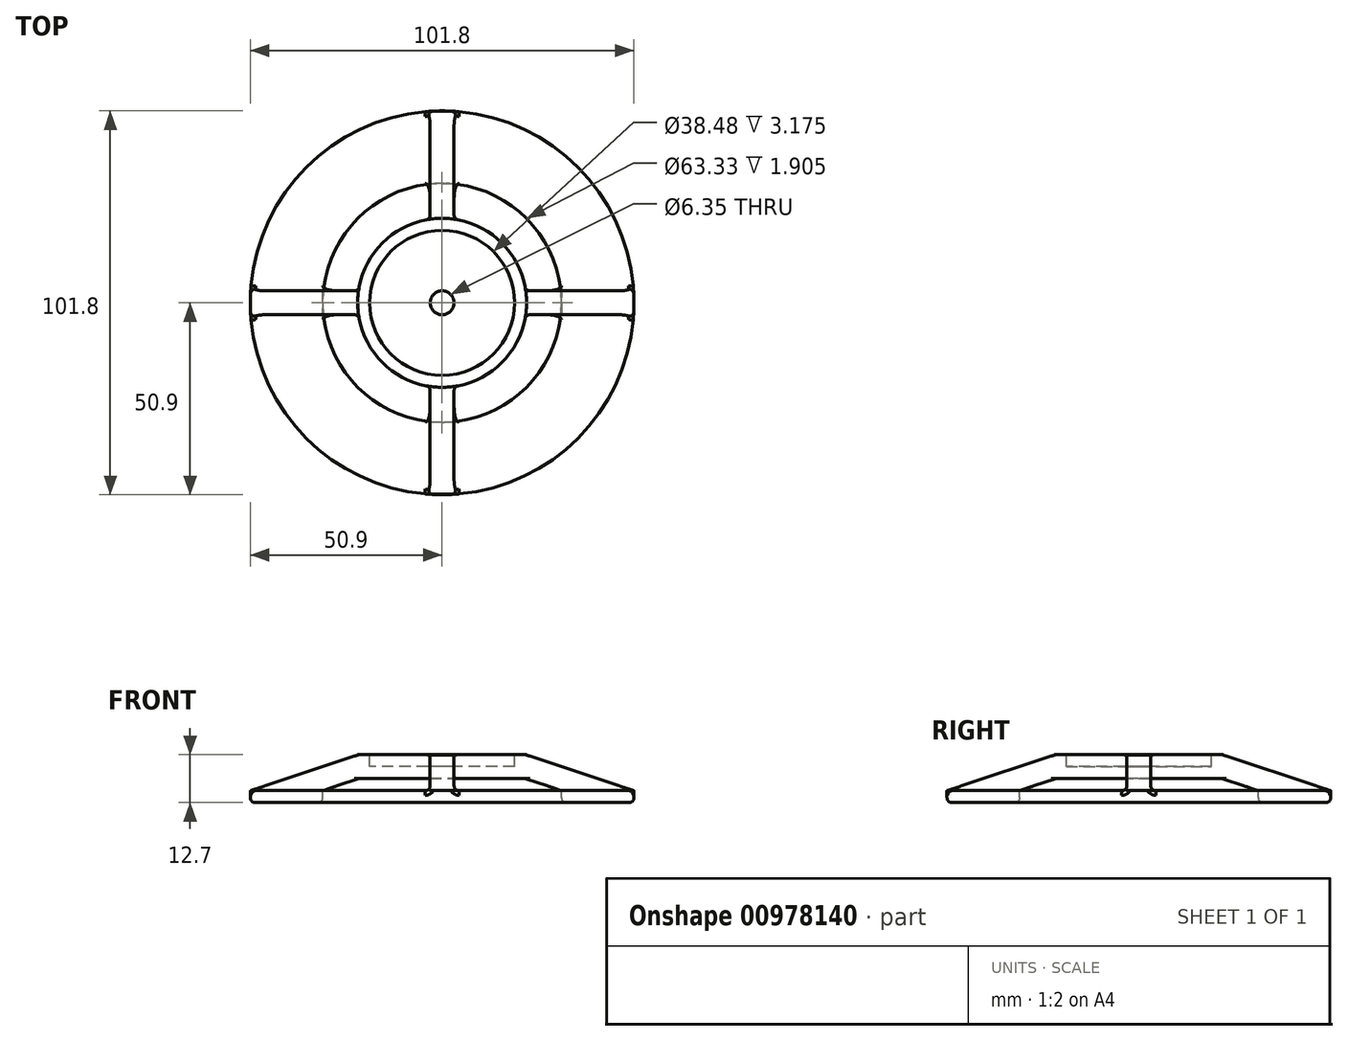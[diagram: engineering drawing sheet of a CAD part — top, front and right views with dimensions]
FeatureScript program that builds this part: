
annotation { "Feature Type Name" : "Feature", "Feature Type Description" : "" }
export const myFeature = defineFeature(function(context is Context, id is Id, definition is map)
    precondition{}
    {
        {
            var Q0;
            Q0=qCreatedBy(makeId("Top.planeOp"),FACE);
            var sketch = newSketch(context, id + "F0", { "sketchPlane" : qUnion([Q0])});
            skCircle(sketch, "E0", {"center": v(0, 0) * mm, "radius": 22.42 * mm});
            skSolve(sketch);
        }
        {
            var Q0;
            Q0 = qSketchRegion(id + "F0", true);
            extrude(context, id + "F1", {"entities" : qUnion([Q0]), "depth" : 6.35 * mm, "offsetDistance" : 25.4 * mm});
        }
        {
            var Q0;
            Q0=makeQuery(id+"F1.opExtrude","CAP_FACE",FACE,{"disambiguationData":[OSD([sQuery(id+"F0.wireOp",EDGE,"E0")])],"isStart":false});
            var sketch = newSketch(context, id + "F2", { "sketchPlane" : qUnion([Q0])});
            skCircle(sketch, "E1", {"center": v(0, 0) * mm, "radius": 19.24 * mm});
            skSolve(sketch);
        }
        {
            var Q0;
            Q0 = qSketchRegion(id + "F2", true);
            extrude(context, id + "F3", {"entities" : qUnion([Q0]), "operationType" : NewBodyOperationType.REMOVE, "oppositeDirection" : true, "depth" : 3.17 * mm, "offsetDistance" : 25.4 * mm});
        }
        {
            var Q0;
            Q0=qCreatedBy(makeId("Front.planeOp"),FACE);
            var sketch = newSketch(context, id + "F4", { "sketchPlane" : qUnion([Q0])});
            skLineSegment(sketch, "E2", {"start": v(-22.1, 6.35) * mm, "end": v(-50.8, -3.18) * mm});
            skLineSegment(sketch, "E3", {"start": v(-50.8, -3.18) * mm, "end": v(-31.67, -3.18) * mm});
            skLineSegment(sketch, "E4", {"start": v(-31.67, -3.18) * mm, "end": v(-22.1, 0) * mm});
            skLineSegment(sketch, "E5", {"start": v(-22.1, 0) * mm, "end": v(-22.1, 6.35) * mm});
            skSolve(sketch);
        }
        {
            var Q0;
            Q0 = qSketchRegion(id + "F4", true);
            extrude(context, id + "F5", {"entities" : qUnion([Q0]), "operationType" : NewBodyOperationType.ADD, "endBound" : BoundingType.SYMMETRIC, "depth" : 6.35 * mm, "offsetDistance" : 25.4 * mm});
        }
        {
            var Q0;
            Q0=qCreatedBy(makeId("Front.planeOp"),FACE);
            var sketch = newSketch(context, id + "F6", { "sketchPlane" : qUnion([Q0])});
            skLineSegment(sketch, "E6", {"start": v(0, 0) * mm, "end": v(0, 12.7) * mm, "construction": true});
            skSolve(sketch);
        }
        {
            var Q0;
            Q0=makeQuery(id+"F1.opExtrude","SWEPT_BODY",BODY,{"disambiguationData":[OSD([sQuery(id+"F0.wireOp",EDGE,"E0")])]});
            var Q1;
            Q1=sQuery(id+"F6.wireOp",EDGE,"E6");
            circularPattern(context, id + "F7", {"entities" : qUnion([Q0]), "axis" : qUnion([Q1]), "angle" : 360 * degree, "instanceCount" : 4, "equalSpace" : true});
        }
        {
            var Q0;
            Q0=makeQuery(id+"F5.opExtrude","SWEPT_FACE",FACE,{"disambiguationData":[OSD([sQuery(id+"F4.wireOp",EDGE,"E3")])]});
            var sketch = newSketch(context, id + "F8", { "sketchPlane" : qUnion([Q0])});
            skCircle(sketch, "E7", {"center": v(0, 0) * mm, "radius": 50.9 * mm});
            skCircle(sketch, "E8", {"center": v(0, 0) * mm, "radius": 31.67 * mm});
            skSolve(sketch);
        }
        {
            var Q0;
            Q0 = qSketchRegion(id + "F8", true);
            extrude(context, id + "F9", {"entities" : qUnion([Q0]), "operationType" : NewBodyOperationType.ADD, "depth" : 3.17 * mm, "offsetDistance" : 25.4 * mm});
        }
        {
            var Q0;
            Q0=makeQuery(id+"F3.boolean.opBoolean","COPY",FACE,{"derivedFrom":makeQuery(id+"F3.opExtrude","CAP_FACE",FACE,{"disambiguationData":[OSD([sQuery(id+"F2.wireOp",EDGE,"E1")])],"isStart":false})});
            var sketch = newSketch(context, id + "F10", { "sketchPlane" : qUnion([Q0])});
            skCircle(sketch, "E9", {"center": v(0, 0) * mm, "radius": 3.18 * mm});
            skSolve(sketch);
        }
        {
            var Q0;
            Q0 = qSketchRegion(id + "F10", true);
            extrude(context, id + "F11", {"entities" : qUnion([Q0]), "operationType" : NewBodyOperationType.REMOVE, "endBound" : BoundingType.THROUGH_ALL, "oppositeDirection" : true, "depth" : 25.4 * mm, "offsetDistance" : 25.4 * mm});
        }
        {
            var Q0;
            Q0=makeQuery(id+"F3.boolean.opBoolean","COPY",EDGE,{"derivedFrom":makeQuery(id+"F3.opExtrude","CAP_EDGE",EDGE,{"disambiguationData":[OSD([sQuery(id+"F2.wireOp",EDGE,"E1")])],"isStart":true})});
            var Q1;
            Q1=makeQuery(id+"F5.opExtrude","CAP_EDGE",EDGE,{"disambiguationData":[OSD([sQuery(id+"F4.wireOp",EDGE,"E3")])],"isStart":false});
            var Q2;
            Q2=makeQuery(id+"F7.opPattern","COPY",EDGE,{"derivedFrom":makeQuery(id+"F5.opExtrude","CAP_EDGE",EDGE,{"disambiguationData":[OSD([sQuery(id+"F4.wireOp",EDGE,"E3")])],"isStart":true}),"instanceName":"1"});
            var Q3;
            Q3=makeQuery(id+"F7.opPattern","COPY",EDGE,{"derivedFrom":makeQuery(id+"F5.opExtrude","CAP_EDGE",EDGE,{"disambiguationData":[OSD([sQuery(id+"F4.wireOp",EDGE,"E3")])],"isStart":false}),"instanceName":"1"});
            var Q4;
            Q4=makeQuery(id+"F7.opPattern","COPY",EDGE,{"derivedFrom":makeQuery(id+"F5.opExtrude","CAP_EDGE",EDGE,{"disambiguationData":[OSD([sQuery(id+"F4.wireOp",EDGE,"E3")])],"isStart":true}),"instanceName":"2"});
            var Q5;
            {var subQ0=makeQuery(id+"F1.opExtrude","SWEPT_FACE",FACE,{"disambiguationData":[OSD([sQuery(id+"F0.wireOp",EDGE,"E0")])]});var subQ1=subQ0;Q5=makeQuery(id+"F9.boolean.opBoolean","INTERSECT",EDGE,{"disambiguationData":[topologyDisambiguationEdgeConnected([makeQuery(id+"F7.opPattern","COPY",FACE,{"derivedFrom":makeQuery(id+"F5.opExtrude","CAP_FACE",FACE,{"disambiguationData":[OSD([sQuery(id+"F4.wireOp",EDGE,"E2"),sQuery(id+"F4.wireOp",EDGE,"E3"),sQuery(id+"F4.wireOp",EDGE,"E4"),sQuery(id+"F4.wireOp",EDGE,"E5")])],"isStart":true}),"instanceName":"2"})])],"derivedFrom":[subQ1,makeQuery(id+"F7.opPattern","COPY",FACE,{"derivedFrom":subQ1,"instanceName":"1"}),makeQuery(id+"F7.opPattern","COPY",FACE,{"derivedFrom":subQ1,"instanceName":"3"})]});}
            var Q6;
            {var subQ0=makeQuery(id+"F1.opExtrude","SWEPT_FACE",FACE,{"disambiguationData":[OSD([sQuery(id+"F0.wireOp",EDGE,"E0")])]});var subQ1=subQ0;Q6=makeQuery(id+"F9.boolean.opBoolean","INTERSECT",EDGE,{"disambiguationData":[topologyDisambiguationEdgeConnected([makeQuery(id+"F7.opPattern","COPY",FACE,{"derivedFrom":makeQuery(id+"F5.opExtrude","CAP_FACE",FACE,{"disambiguationData":[OSD([sQuery(id+"F4.wireOp",EDGE,"E2"),sQuery(id+"F4.wireOp",EDGE,"E3"),sQuery(id+"F4.wireOp",EDGE,"E4"),sQuery(id+"F4.wireOp",EDGE,"E5")])],"isStart":false}),"instanceName":"1"})])],"derivedFrom":[subQ1,makeQuery(id+"F7.opPattern","COPY",FACE,{"derivedFrom":subQ1,"instanceName":"2"})]});}
            var Q7;
            Q7=makeQuery(id+"F5.boolean.opBoolean","INTERSECT",EDGE,{"derivedFrom":[makeQuery(id+"F1.opExtrude","SWEPT_FACE",FACE,{"disambiguationData":[OSD([sQuery(id+"F0.wireOp",EDGE,"E0")])]}),makeQuery(id+"F5.opExtrude","CAP_FACE",FACE,{"disambiguationData":[OSD([sQuery(id+"F4.wireOp",EDGE,"E2"),sQuery(id+"F4.wireOp",EDGE,"E3"),sQuery(id+"F4.wireOp",EDGE,"E4"),sQuery(id+"F4.wireOp",EDGE,"E5")])],"isStart":false})]});
            var Q8;
            {var subQ0=makeQuery(id+"F1.opExtrude","SWEPT_FACE",FACE,{"disambiguationData":[OSD([sQuery(id+"F0.wireOp",EDGE,"E0")])]});var subQ1=subQ0;Q8=makeQuery(id+"F9.boolean.opBoolean","INTERSECT",EDGE,{"disambiguationData":[topologyDisambiguationEdgeConnected([makeQuery(id+"F7.opPattern","COPY",FACE,{"derivedFrom":makeQuery(id+"F5.opExtrude","CAP_FACE",FACE,{"disambiguationData":[OSD([sQuery(id+"F4.wireOp",EDGE,"E2"),sQuery(id+"F4.wireOp",EDGE,"E3"),sQuery(id+"F4.wireOp",EDGE,"E4"),sQuery(id+"F4.wireOp",EDGE,"E5")])],"isStart":true}),"instanceName":"1"})])],"derivedFrom":[subQ1,makeQuery(id+"F7.opPattern","COPY",FACE,{"derivedFrom":subQ1,"instanceName":"2"})]});}
            var Q9;
            Q9=makeQuery(id+"F5.boolean.opBoolean","INTERSECT",EDGE,{"derivedFrom":[makeQuery(id+"F1.opExtrude","SWEPT_FACE",FACE,{"disambiguationData":[OSD([sQuery(id+"F0.wireOp",EDGE,"E0")])]}),makeQuery(id+"F5.opExtrude","CAP_FACE",FACE,{"disambiguationData":[OSD([sQuery(id+"F4.wireOp",EDGE,"E2"),sQuery(id+"F4.wireOp",EDGE,"E3"),sQuery(id+"F4.wireOp",EDGE,"E4"),sQuery(id+"F4.wireOp",EDGE,"E5")])],"isStart":true})]});
            var Q10;
            Q10=makeQuery(id+"F5.opExtrude","CAP_EDGE",EDGE,{"disambiguationData":[OSD([sQuery(id+"F4.wireOp",EDGE,"E3")])],"isStart":true});
            var Q11;
            {var subQ0=makeQuery(id+"F1.opExtrude","SWEPT_FACE",FACE,{"disambiguationData":[OSD([sQuery(id+"F0.wireOp",EDGE,"E0")])]});var subQ1=subQ0;Q11=makeQuery(id+"F9.boolean.opBoolean","INTERSECT",EDGE,{"disambiguationData":[topologyDisambiguationEdgeConnected([makeQuery(id+"F7.opPattern","COPY",FACE,{"derivedFrom":makeQuery(id+"F5.opExtrude","CAP_FACE",FACE,{"disambiguationData":[OSD([sQuery(id+"F4.wireOp",EDGE,"E2"),sQuery(id+"F4.wireOp",EDGE,"E3"),sQuery(id+"F4.wireOp",EDGE,"E4"),sQuery(id+"F4.wireOp",EDGE,"E5")])],"isStart":false}),"instanceName":"3"})])],"derivedFrom":[subQ1,makeQuery(id+"F7.opPattern","COPY",FACE,{"derivedFrom":subQ1,"instanceName":"1"}),makeQuery(id+"F7.opPattern","COPY",FACE,{"derivedFrom":subQ1,"instanceName":"2"})]});}
            var Q12;
            Q12=makeQuery(id+"F7.opPattern","COPY",EDGE,{"derivedFrom":makeQuery(id+"F5.opExtrude","CAP_EDGE",EDGE,{"disambiguationData":[OSD([sQuery(id+"F4.wireOp",EDGE,"E3")])],"isStart":false}),"instanceName":"3"});
            var Q13;
            {var subQ0=makeQuery(id+"F1.opExtrude","SWEPT_FACE",FACE,{"disambiguationData":[OSD([sQuery(id+"F0.wireOp",EDGE,"E0")])]});var subQ1=subQ0;Q13=makeQuery(id+"F9.boolean.opBoolean","INTERSECT",EDGE,{"disambiguationData":[topologyDisambiguationEdgeConnected([makeQuery(id+"F7.opPattern","COPY",FACE,{"derivedFrom":makeQuery(id+"F5.opExtrude","CAP_FACE",FACE,{"disambiguationData":[OSD([sQuery(id+"F4.wireOp",EDGE,"E2"),sQuery(id+"F4.wireOp",EDGE,"E3"),sQuery(id+"F4.wireOp",EDGE,"E4"),sQuery(id+"F4.wireOp",EDGE,"E5")])],"isStart":true}),"instanceName":"3"})])],"derivedFrom":[subQ1,makeQuery(id+"F7.opPattern","COPY",FACE,{"derivedFrom":subQ1,"instanceName":"1"}),makeQuery(id+"F7.opPattern","COPY",FACE,{"derivedFrom":subQ1,"instanceName":"2"})]});}
            var Q14;
            Q14=makeQuery(id+"F7.opPattern","COPY",EDGE,{"derivedFrom":makeQuery(id+"F5.opExtrude","CAP_EDGE",EDGE,{"disambiguationData":[OSD([sQuery(id+"F4.wireOp",EDGE,"E3")])],"isStart":true}),"instanceName":"3"});
            var Q15;
            {var subQ0=makeQuery(id+"F1.opExtrude","SWEPT_FACE",FACE,{"disambiguationData":[OSD([sQuery(id+"F0.wireOp",EDGE,"E0")])]});var subQ1=subQ0;Q15=makeQuery(id+"F9.boolean.opBoolean","INTERSECT",EDGE,{"disambiguationData":[topologyDisambiguationEdgeConnected([makeQuery(id+"F7.opPattern","COPY",FACE,{"derivedFrom":makeQuery(id+"F5.opExtrude","CAP_FACE",FACE,{"disambiguationData":[OSD([sQuery(id+"F4.wireOp",EDGE,"E2"),sQuery(id+"F4.wireOp",EDGE,"E3"),sQuery(id+"F4.wireOp",EDGE,"E4"),sQuery(id+"F4.wireOp",EDGE,"E5")])],"isStart":false}),"instanceName":"2"})])],"derivedFrom":[subQ1,makeQuery(id+"F7.opPattern","COPY",FACE,{"derivedFrom":subQ1,"instanceName":"1"}),makeQuery(id+"F7.opPattern","COPY",FACE,{"derivedFrom":subQ1,"instanceName":"3"})]});}
            var Q16;
            Q16=makeQuery(id+"F7.opPattern","COPY",EDGE,{"derivedFrom":makeQuery(id+"F5.opExtrude","CAP_EDGE",EDGE,{"disambiguationData":[OSD([sQuery(id+"F4.wireOp",EDGE,"E3")])],"isStart":false}),"instanceName":"2"});
            var Q17;
            Q17=makeQuery(id+"F11.boolean.opBoolean","INTERSECT",EDGE,{"derivedFrom":[makeQuery(id+"F1.opExtrude","CAP_FACE",FACE,{"disambiguationData":[OSD([sQuery(id+"F0.wireOp",EDGE,"E0")])],"isStart":true}),makeQuery(id+"F11.opExtrude","SWEPT_FACE",FACE,{"disambiguationData":[OSD([sQuery(id+"F10.wireOp",EDGE,"E9")])]})]});
            var Q18;
            {var subQ0=makeQuery(id+"F1.opExtrude","CAP_FACE",FACE,{"disambiguationData":[OSD([sQuery(id+"F0.wireOp",EDGE,"E0")])],"isStart":true});var subQ1=subQ0;Q18=makeQuery(id+"F9.boolean.opBoolean","INTERSECT",EDGE,{"disambiguationData":[topologyDisambiguationEdgeConnected([makeQuery(id+"F7.opPattern","COPY",FACE,{"derivedFrom":makeQuery(id+"F5.opExtrude","SWEPT_FACE",FACE,{"disambiguationData":[OSD([sQuery(id+"F4.wireOp",EDGE,"E4")])]}),"instanceName":"1"})])],"derivedFrom":[subQ1,makeQuery(id+"F7.opPattern","COPY",FACE,{"derivedFrom":subQ1,"instanceName":"2"})]});}
            var Q19;
            {var subQ0=makeQuery(id+"F1.opExtrude","CAP_FACE",FACE,{"disambiguationData":[OSD([sQuery(id+"F0.wireOp",EDGE,"E0")])],"isStart":true});var subQ1=subQ0;Q19=makeQuery(id+"F9.boolean.opBoolean","INTERSECT",EDGE,{"disambiguationData":[topologyDisambiguationEdgeConnected([makeQuery(id+"F7.opPattern","COPY",FACE,{"derivedFrom":makeQuery(id+"F5.opExtrude","SWEPT_FACE",FACE,{"disambiguationData":[OSD([sQuery(id+"F4.wireOp",EDGE,"E4")])]}),"instanceName":"2"})])],"derivedFrom":[subQ1,makeQuery(id+"F7.opPattern","COPY",FACE,{"derivedFrom":subQ1,"instanceName":"1"}),makeQuery(id+"F7.opPattern","COPY",FACE,{"derivedFrom":subQ1,"instanceName":"3"})]});}
            var Q20;
            {var subQ0=makeQuery(id+"F1.opExtrude","CAP_FACE",FACE,{"disambiguationData":[OSD([sQuery(id+"F0.wireOp",EDGE,"E0")])],"isStart":true});var subQ1=subQ0;Q20=makeQuery(id+"F9.boolean.opBoolean","INTERSECT",EDGE,{"disambiguationData":[topologyDisambiguationEdgeConnected([makeQuery(id+"F7.opPattern","COPY",FACE,{"derivedFrom":makeQuery(id+"F5.opExtrude","SWEPT_FACE",FACE,{"disambiguationData":[OSD([sQuery(id+"F4.wireOp",EDGE,"E4")])]}),"instanceName":"3"})])],"derivedFrom":[subQ1,makeQuery(id+"F7.opPattern","COPY",FACE,{"derivedFrom":subQ1,"instanceName":"1"}),makeQuery(id+"F7.opPattern","COPY",FACE,{"derivedFrom":subQ1,"instanceName":"2"})]});}
            var Q21;
            Q21=makeQuery(id+"F5.opExtrude","SWEPT_EDGE",EDGE,{"disambiguationData":[OSD([sQuery(id+"F4.wireOp",EDGE,"E4"),sQuery(id+"F4.wireOp",EDGE,"E5")])]});
            var Q22;
            Q22=makeQuery(id+"F9.opExtrude","CAP_FACE",FACE,{"disambiguationData":[OSD([sQuery(id+"F8.wireOp",EDGE,"E7"),sQuery(id+"F8.wireOp",EDGE,"E8")])],"isStart":false});
            fillet(context, id + "F12", {"entities" : qUnion([Q0, Q1, Q2, Q3, Q4, Q5, Q6, Q7, Q8, Q9, Q10, Q11, Q12, Q13, Q14, Q15, Q16, Q17, Q18, Q19, Q20, Q21, Q22]), "radius" : 1.27 * mm, "tangentPropagation" : true, "allowEdgeOverflow" : false});
        }
        {
            var Q0;
            {var subQ0=sQuery(id+"F4.wireOp",EDGE,"E5");var subQ1=sQuery(id+"F4.wireOp",EDGE,"E4");var subQ2=sQuery(id+"F4.wireOp",EDGE,"E3");var subQ3=sQuery(id+"F4.wireOp",EDGE,"E2");var subQ4=sQuery(id+"F8.wireOp",EDGE,"E7");var subQ5=makeQuery(id+"F5.opExtrude","SWEPT_FACE",FACE,{"disambiguationData":[OSD([subQ3])]});Q0=makeQuery(id+"F9.boolean.opBoolean","SPLIT",EDGE,{"disambiguationData":[TD([subQ5,makeQuery(id+"F5.opExtrude","CAP_FACE",FACE,{"disambiguationData":[OSD([subQ3,subQ2,subQ1,subQ0])],"isStart":false}),makeQuery(id+"F7.opPattern","COPY",FACE,{"derivedFrom":subQ5,"instanceName":"1"}),makeQuery(id+"F7.opPattern","COPY",FACE,{"derivedFrom":makeQuery(id+"F5.opExtrude","CAP_FACE",FACE,{"disambiguationData":[OSD([subQ3,subQ2,subQ1,subQ0])],"isStart":true}),"instanceName":"1"}),makeQuery(id+"F9.opExtrude","SWEPT_FACE",FACE,{"disambiguationData":[OSD([subQ4])]}),makeQuery(id+"F9.opExtrude","CAP_FACE",FACE,{"disambiguationData":[OSD([subQ4,sQuery(id+"F8.wireOp",EDGE,"E8")])],"isStart":true})])],"derivedFrom":makeQuery(id+"F9.opExtrude","CAP_EDGE",EDGE,{"disambiguationData":[OSD([subQ4])],"isStart":true})});}
            var Q1;
            {var subQ0=sQuery(id+"F4.wireOp",EDGE,"E5");var subQ1=sQuery(id+"F4.wireOp",EDGE,"E4");var subQ2=sQuery(id+"F4.wireOp",EDGE,"E3");var subQ3=sQuery(id+"F4.wireOp",EDGE,"E2");var subQ4=makeQuery(id+"F5.opExtrude","SWEPT_FACE",FACE,{"disambiguationData":[OSD([subQ3])]});var subQ5=sQuery(id+"F8.wireOp",EDGE,"E7");Q1=makeQuery(id+"F9.boolean.opBoolean","SPLIT",EDGE,{"disambiguationData":[TD([makeQuery(id+"F7.opPattern","COPY",FACE,{"derivedFrom":subQ4,"instanceName":"1"}),makeQuery(id+"F7.opPattern","COPY",FACE,{"derivedFrom":makeQuery(id+"F5.opExtrude","CAP_FACE",FACE,{"disambiguationData":[OSD([subQ3,subQ2,subQ1,subQ0])],"isStart":false}),"instanceName":"1"}),makeQuery(id+"F7.opPattern","COPY",FACE,{"derivedFrom":subQ4,"instanceName":"2"}),makeQuery(id+"F7.opPattern","COPY",FACE,{"derivedFrom":makeQuery(id+"F5.opExtrude","CAP_FACE",FACE,{"disambiguationData":[OSD([subQ3,subQ2,subQ1,subQ0])],"isStart":true}),"instanceName":"2"}),makeQuery(id+"F9.opExtrude","SWEPT_FACE",FACE,{"disambiguationData":[OSD([subQ5])]}),makeQuery(id+"F9.opExtrude","CAP_FACE",FACE,{"disambiguationData":[OSD([subQ5,sQuery(id+"F8.wireOp",EDGE,"E8")])],"isStart":true})])],"derivedFrom":makeQuery(id+"F9.opExtrude","CAP_EDGE",EDGE,{"disambiguationData":[OSD([subQ5])],"isStart":true})});}
            var Q2;
            {var subQ0=sQuery(id+"F4.wireOp",EDGE,"E5");var subQ1=sQuery(id+"F4.wireOp",EDGE,"E4");var subQ2=sQuery(id+"F4.wireOp",EDGE,"E3");var subQ3=sQuery(id+"F4.wireOp",EDGE,"E2");var subQ4=makeQuery(id+"F5.opExtrude","SWEPT_FACE",FACE,{"disambiguationData":[OSD([subQ3])]});var subQ5=sQuery(id+"F8.wireOp",EDGE,"E7");Q2=makeQuery(id+"F9.boolean.opBoolean","SPLIT",EDGE,{"disambiguationData":[TD([makeQuery(id+"F7.opPattern","COPY",FACE,{"derivedFrom":subQ4,"instanceName":"2"}),makeQuery(id+"F7.opPattern","COPY",FACE,{"derivedFrom":makeQuery(id+"F5.opExtrude","CAP_FACE",FACE,{"disambiguationData":[OSD([subQ3,subQ2,subQ1,subQ0])],"isStart":false}),"instanceName":"2"}),makeQuery(id+"F7.opPattern","COPY",FACE,{"derivedFrom":subQ4,"instanceName":"3"}),makeQuery(id+"F7.opPattern","COPY",FACE,{"derivedFrom":makeQuery(id+"F5.opExtrude","CAP_FACE",FACE,{"disambiguationData":[OSD([subQ3,subQ2,subQ1,subQ0])],"isStart":true}),"instanceName":"3"}),makeQuery(id+"F9.opExtrude","SWEPT_FACE",FACE,{"disambiguationData":[OSD([subQ5])]}),makeQuery(id+"F9.opExtrude","CAP_FACE",FACE,{"disambiguationData":[OSD([subQ5,sQuery(id+"F8.wireOp",EDGE,"E8")])],"isStart":true})])],"derivedFrom":makeQuery(id+"F9.opExtrude","CAP_EDGE",EDGE,{"disambiguationData":[OSD([subQ5])],"isStart":true})});}
            var Q3;
            {var subQ0=sQuery(id+"F4.wireOp",EDGE,"E5");var subQ1=sQuery(id+"F4.wireOp",EDGE,"E4");var subQ2=sQuery(id+"F4.wireOp",EDGE,"E3");var subQ3=sQuery(id+"F4.wireOp",EDGE,"E2");var subQ4=makeQuery(id+"F5.opExtrude","SWEPT_FACE",FACE,{"disambiguationData":[OSD([subQ3])]});var subQ5=sQuery(id+"F8.wireOp",EDGE,"E7");Q3=makeQuery(id+"F9.boolean.opBoolean","SPLIT",EDGE,{"disambiguationData":[TD([subQ4,makeQuery(id+"F5.opExtrude","CAP_FACE",FACE,{"disambiguationData":[OSD([subQ3,subQ2,subQ1,subQ0])],"isStart":true}),makeQuery(id+"F7.opPattern","COPY",FACE,{"derivedFrom":subQ4,"instanceName":"3"}),makeQuery(id+"F7.opPattern","COPY",FACE,{"derivedFrom":makeQuery(id+"F5.opExtrude","CAP_FACE",FACE,{"disambiguationData":[OSD([subQ3,subQ2,subQ1,subQ0])],"isStart":false}),"instanceName":"3"}),makeQuery(id+"F9.opExtrude","SWEPT_FACE",FACE,{"disambiguationData":[OSD([subQ5])]}),makeQuery(id+"F9.opExtrude","CAP_FACE",FACE,{"disambiguationData":[OSD([subQ5,sQuery(id+"F8.wireOp",EDGE,"E8")])],"isStart":true})])],"derivedFrom":makeQuery(id+"F9.opExtrude","CAP_EDGE",EDGE,{"disambiguationData":[OSD([subQ5])],"isStart":true})});}
            fillet(context, id + "F13", {"entities" : qUnion([Q0, Q1, Q2, Q3]), "radius" : 1.27 * mm, "tangentPropagation" : true, "allowEdgeOverflow" : false});
        }
    });
